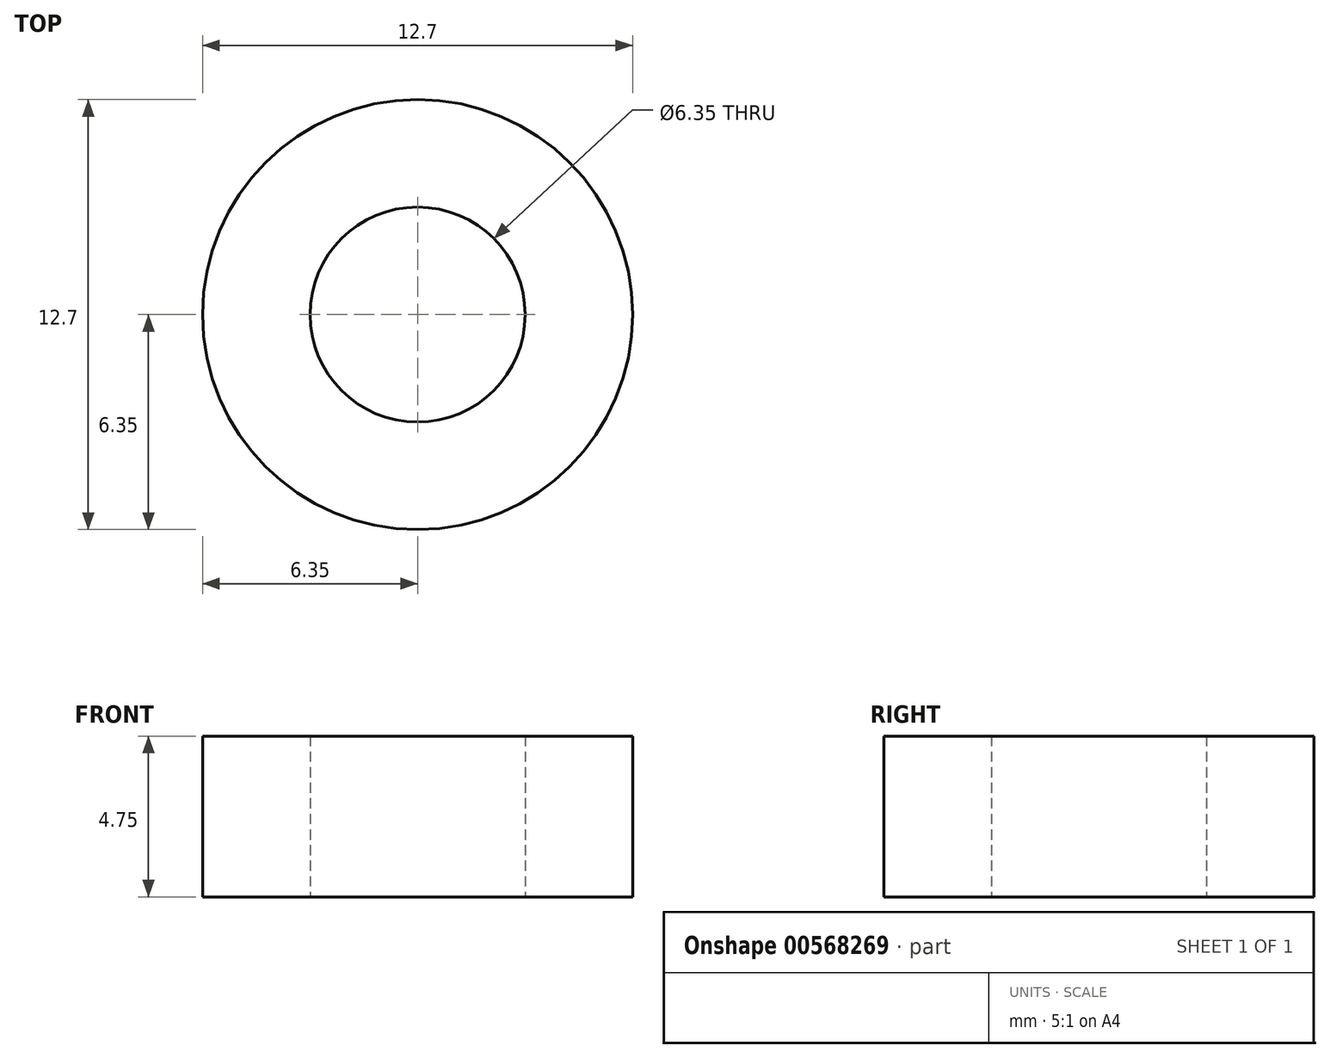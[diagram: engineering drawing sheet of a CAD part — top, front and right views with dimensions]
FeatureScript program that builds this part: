
annotation { "Feature Type Name" : "Feature", "Feature Type Description" : "" }
export const myFeature = defineFeature(function(context is Context, id is Id, definition is map)
    precondition{}
    {
        {
            var Q0;
            Q0=qCreatedBy(makeId("Top.planeOp"),FACE);
            var sketch = newSketch(context, id + "F0", { "sketchPlane" : qUnion([Q0])});
            skCircle(sketch, "E0", {"center": v(0, 0) * mm, "radius": 6.35 * mm});
            skCircle(sketch, "E1", {"center": v(0, 0) * mm, "radius": 3.18 * mm});
            skSolve(sketch);
        }
        {
            var Q0;
            Q0=makeQuery(id+"F0.imprint","IMPRINT",FACE,{"disambiguationData":[TD([[makeQuery(id+"F0.imprint","IMPRINT",EDGE,{"derivedFrom":sQuery(id+"F0.wireOp",EDGE,"E0")}),1.0]])]});
            extrude(context, id + "F1", {"entities" : qUnion([Q0]), "depth" : 4.75 * mm, "offsetDistance" : 25 * mm});
        }
    });
